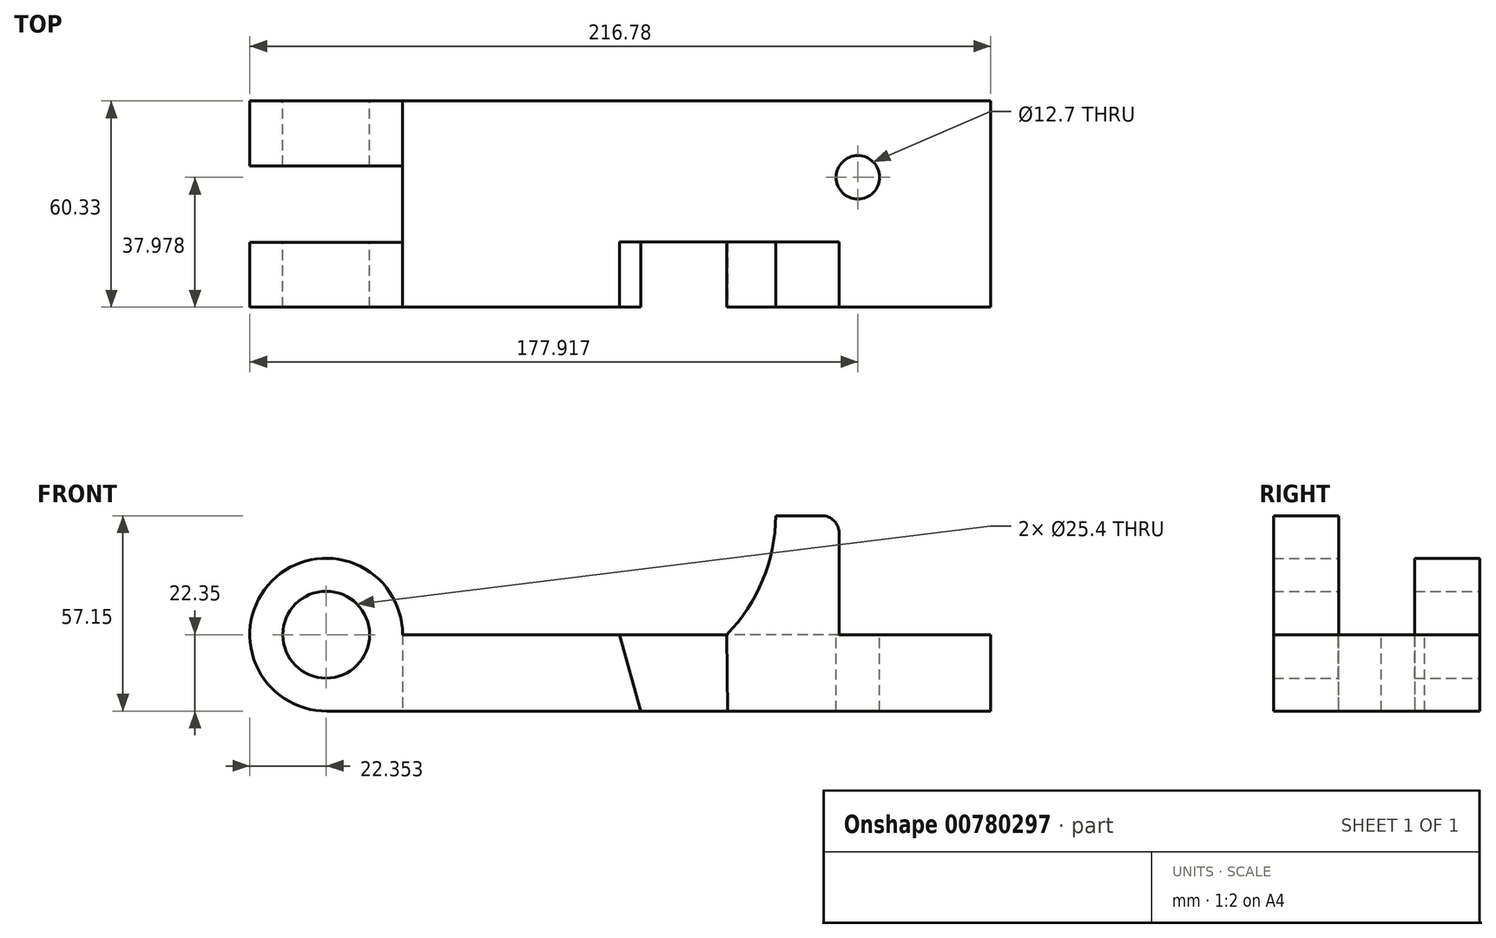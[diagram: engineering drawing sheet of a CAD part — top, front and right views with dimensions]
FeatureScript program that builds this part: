
annotation { "Feature Type Name" : "Feature", "Feature Type Description" : "" }
export const myFeature = defineFeature(function(context is Context, id is Id, definition is map)
    precondition{}
    {
        {
            var Q0;
            Q0=qCreatedBy(makeId("Front.planeOp"),FACE);
            var sketch = newSketch(context, id + "F0", { "sketchPlane" : qUnion([Q0])});
            skCircle(sketch, "E0", {"center": v(-48.99, 0) * mm, "radius": 12.7 * mm});
            skArc(sketch, "E1", {"start": v(-26.63, 0) * mm, "mid": v(-64.87, 15.73) * mm, "end": v(-48.77, -22.35) * mm});
            skLineSegment(sketch, "E2", {"start": v(145.22, 0) * mm, "end": v(-26.63, 0) * mm});
            skPoint(sketch, "E3.start.orphan", {"position": v(-48.77, -22.35) * mm});
            skPoint(sketch, "E4.start.orphan", {"position": v(43.08, -21.46) * mm});
            skLineSegment(sketch, "E5", {"start": v(-48.77, -22.35) * mm, "end": v(145.44, -22.35) * mm});
            skPoint(sketch, "E6.end.orphan", {"position": v(145.44, 0) * mm});
            skLineSegment(sketch, "E7", {"start": v(145.44, 0) * mm, "end": v(145.44, -22.35) * mm});
            skLineSegment(sketch, "E8", {"start": v(43.08, -22.35) * mm, "end": v(36.87, 0) * mm});
            skLineSegment(sketch, "E9", {"start": v(68.26, 0) * mm, "end": v(68.48, -22.35) * mm});
            skLineSegment(sketch, "E10", {"start": v(145.22, 0) * mm, "end": v(145.44, 0) * mm});
            skLineSegment(sketch, "E11", {"start": v(101.1, 0) * mm, "end": v(101.1, 34.8) * mm});
            skLineSegment(sketch, "E12", {"start": v(101.1, 34.8) * mm, "end": v(82.55, 34.8) * mm});
            skArc(sketch, "E13.trimOffspring", {"start": v(68.26, 0) * mm, "mid": v(78.74, 16.03) * mm, "end": v(82.55, 34.8) * mm});
            skSolve(sketch);
        }
        {
            var Q0;
            Q0 = qSketchRegion(id + "F0", true);
            extrude(context, id + "F1", {"entities" : qUnion([Q0]), "depth" : 60.32 * mm, "offsetDistance" : 25.4 * mm});
        }
        {
            var Q0;
            Q0 = qSketchRegion(id + "F0", true);
            extrude(context, id + "F2", {"entities" : qUnion([Q0]), "operationType" : NewBodyOperationType.ADD, "depth" : 25.4 * mm, "offsetDistance" : 25.4 * mm});
        }
        {
            var Q0;
            Q0=makeQuery(id+"F1.opExtrude","CAP_FACE",FACE,{"disambiguationData":[OSD([sQuery(id+"F0.wireOp",EDGE,"E0"),sQuery(id+"F0.wireOp",EDGE,"E1"),sQuery(id+"F0.wireOp",EDGE,"E2"),sQuery(id+"F0.wireOp",EDGE,"E5"),sQuery(id+"F0.wireOp",EDGE,"E7"),sQuery(id+"F0.wireOp",EDGE,"E10"),sQuery(id+"F0.wireOp",EDGE,"E11"),sQuery(id+"F0.wireOp",EDGE,"E12"),sQuery(id+"F0.wireOp",EDGE,"E13.trimOffspring")])],"isStart":false});
            var sketch = newSketch(context, id + "F3", { "sketchPlane" : qUnion([Q0])});
            skCircle(sketch, "E14", {"center": v(-48.99, 0) * mm, "radius": 12.7 * mm});
            skArc(sketch, "E15", {"start": v(-26.63, 0) * mm, "mid": v(-64.87, 15.73) * mm, "end": v(-48.77, -22.35) * mm});
            skLineSegment(sketch, "E16", {"start": v(145.22, 0) * mm, "end": v(-26.63, 0) * mm});
            skPoint(sketch, "E17.start.orphan", {"position": v(-48.77, -22.35) * mm});
            skPoint(sketch, "E18.start.orphan", {"position": v(43.08, -33.98) * mm});
            skLineSegment(sketch, "E19", {"start": v(-48.77, -22.35) * mm, "end": v(145.44, -22.35) * mm});
            skPoint(sketch, "E20.end.orphan", {"position": v(145.44, 0) * mm});
            skLineSegment(sketch, "E21", {"start": v(145.44, 0) * mm, "end": v(145.44, -22.35) * mm});
            skLineSegment(sketch, "E22", {"start": v(43.08, -22.35) * mm, "end": v(36.87, 0) * mm});
            skLineSegment(sketch, "E23", {"start": v(68.26, 0) * mm, "end": v(68.48, -22.35) * mm});
            skLineSegment(sketch, "E24", {"start": v(145.22, 0) * mm, "end": v(145.44, 0) * mm});
            skLineSegment(sketch, "E25", {"start": v(101.1, 0) * mm, "end": v(101.1, 34.8) * mm});
            skSolve(sketch);
        }
        {
            var Q0;
            {var subQ2=sQuery(id+"F3.wireOp",EDGE,"E22");Q0=makeQuery(id+"F3.imprint","IMPRINT",FACE,{"disambiguationData":[TD([[makeQuery(id+"F3.imprint","IMPRINT",EDGE,{"derivedFrom":subQ2}),-1.0]])]});}
            extrude(context, id + "F4", {"entities" : qUnion([Q0]), "operationType" : NewBodyOperationType.REMOVE, "oppositeDirection" : true, "depth" : 19.05 * mm, "offsetDistance" : 25.4 * mm});
        }
        {
            var Q0;
            {var subQ2=sQuery(id+"F0.wireOp",EDGE,"E11");Q0=makeQuery(id+"F0.imprint","IMPRINT",FACE,{"disambiguationData":[TD([[makeQuery(id+"F0.imprint","IMPRINT",EDGE,{"derivedFrom":subQ2}),1.0]])]});}
            extrude(context, id + "F5", {"entities" : qUnion([Q0]), "operationType" : NewBodyOperationType.REMOVE, "depth" : 41.27 * mm, "offsetDistance" : 25.4 * mm});
        }
        {
            var Q0;
            Q0=makeQuery(id+"F1.opExtrude","SWEPT_EDGE",EDGE,{"disambiguationData":[OSD([sQuery(id+"F0.wireOp",EDGE,"E11"),sQuery(id+"F0.wireOp",EDGE,"E12")])]});
            fillet(context, id + "F6", {"entities" : qUnion([Q0]), "radius" : 5.08 * mm, "tangentPropagation" : true, "allowEdgeOverflow" : false});
        }
        {
            var Q0;
            {var subQ0=sQuery(id+"F0.wireOp",EDGE,"E2");Q0=makeQuery(id+"F5.boolean.opBoolean","MERGE",FACE,{"derivedFrom":[makeQuery(id+"F1.opExtrude","SWEPT_FACE",FACE,{"disambiguationData":[OSD([subQ0,sQuery(id+"F0.wireOp",EDGE,"E10")])]}),makeQuery(id+"F1.opExtrude","SWEPT_FACE",FACE,{"disambiguationData":[OSD([subQ0])]}),makeQuery(id+"F5.opExtrude","SWEPT_FACE",FACE,{"disambiguationData":[OSD([subQ0])]})]});}
            var sketch = newSketch(context, id + "F7", { "sketchPlane" : qUnion([Q0])});
            skCircle(sketch, "E26", {"center": v(106.58, -22.35) * mm, "radius": 6.35 * mm});
            skSolve(sketch);
        }
        {
            var Q0;
            Q0=makeQuery(id+"F7.imprint","IMPRINT",FACE,{"disambiguationData":[TD([[makeQuery(id+"F7.imprint","IMPRINT",EDGE,{"derivedFrom":sQuery(id+"F7.wireOp",EDGE,"E26")}),1.0]])]});
            extrude(context, id + "F8", {"entities" : qUnion([Q0]), "operationType" : NewBodyOperationType.REMOVE, "oppositeDirection" : true, "depth" : 25.4 * mm, "offsetDistance" : 25.4 * mm});
        }
        {
            var Q0;
            Q0=qCreatedBy(makeId("Top.planeOp"),FACE);
            var sketch = newSketch(context, id + "F9", { "sketchPlane" : qUnion([Q0])});
            skLineSegment(sketch, "E27.bottom", {"start": v(-26.63, -19) * mm, "end": v(-71.34, -19) * mm});
            skLineSegment(sketch, "E27.top", {"start": v(-26.63, -41.33) * mm, "end": v(-71.34, -41.33) * mm});
            skLineSegment(sketch, "E27.left", {"start": v(-26.63, -19) * mm, "end": v(-26.63, -41.33) * mm});
            skLineSegment(sketch, "E27.right", {"start": v(-71.34, -19) * mm, "end": v(-71.34, -41.33) * mm});
            skSolve(sketch);
        }
        {
            var Q0;
            Q0 = qSketchRegion(id + "F9", true);
            extrude(context, id + "F10", {"entities" : qUnion([Q0]), "operationType" : NewBodyOperationType.REMOVE, "depth" : 25.4 * mm, "offsetDistance" : 25.4 * mm, "hasSecondDirection" : true, "secondDirectionOppositeDirection" : true, "secondDirectionDepth" : 25.4 * mm});
        }
    });
